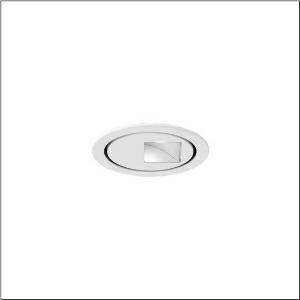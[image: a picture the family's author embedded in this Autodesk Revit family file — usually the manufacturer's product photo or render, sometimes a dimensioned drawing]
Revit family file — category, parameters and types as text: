
# Revit family: lunis_11_micro_round_51dj11cd1wf21
name_source: partatom
category: Lighting Fixtures
units: mm (PartAtom-declared; Revit-internal decimal feet)

## family parameters
Cut with Voids When Loaded = No
Host = Face
Light Source = No
Part Type = Normal
Room Calculation Point = No
Round Connector Dimension = Use Diameter
Shared = No

## types (1)
- Lunis 11 micro round (1 x LED 3000K / CRI = 80 (unbekannt), 1320 lm, 3000K)
    Apparent Load = 20 VA
    CIE Flux Codes = 42 75 96 100 100
    Color Rendering = 80
    Color Temperature = 3000K
    Default Elevation = 1800 mm
    Description = Lunis 11 micro round, downlight, light control with wallwasher, of highly reflective aluminium, highly specular, light emission: direct distribution, LED rated luminous flux: 1.320lm, light colour: 830, with terminal, 5-pole, mains connection: 220..230V, AC, 50/60Hz, LED module, of aluminium, highly specular, white, diameter: 114mm, clamping range: 1..40mm, recessing ring, of plastic, traffic white (RAL 9016), protection rating (complete): IP20, insulation class (complete): insulation class II (safety insulation), certification: CE, permissible ambient temperature for indoor applications: 0..+35°C, packaging unit: 1 piece
    Height = 0 mm  [stored 0 ft]
    Lamp = 1 x LED 3000K / CRI >= 80 (unbekannt)
    Lamp Light Flux = 1320 lm
    Lamp count = 1
    Length = 114 mm
    Luminous efficacy = 67 lm/W
    Manufacturer = Siteco
    ModVariant = No
    Model = 51DJ11CD1WF21
    Mounting Place = Ceiling
    Mounting Type = Recessed
    Number of Poles = 1
    OnlyDefault = Yes
    Power Factor = 1
    Product Name = Lunis 11 micro round
    Product group = downlight
    ProductGroupID = 401
    Protection Class = Protection class II
    Protection Degree = IP 20
    RLX_Detail_Level = 1
    RLX_Emergency_Light_Flux = 0 lm
    RLX_Emergency_Type = 0
    RLX_Emergency_Type_DB = No
    RlxData = <blob elided: 40405 chars, md5=eace1fb1>
    Socket = socket
    Standby Power = 0 W
    System Light Flux = 1320 lm
    System Power = 20 W
    Type Comments = Product without accessories
    Type Image = l_1004773.jpg
    URL = http://relux.com
    VarID = ---
    Voltage = 0 V
    Weight = 0.00 kg
    Width = 114 mm

note: [stored X ft] marks values corroborated as IEEE doubles in the binary element streams (Revit-internal decimal feet)

## geometry (parser evidence)
native form markers: Blend x4, Sweep x8
no freeform markers — native parametric forms only
